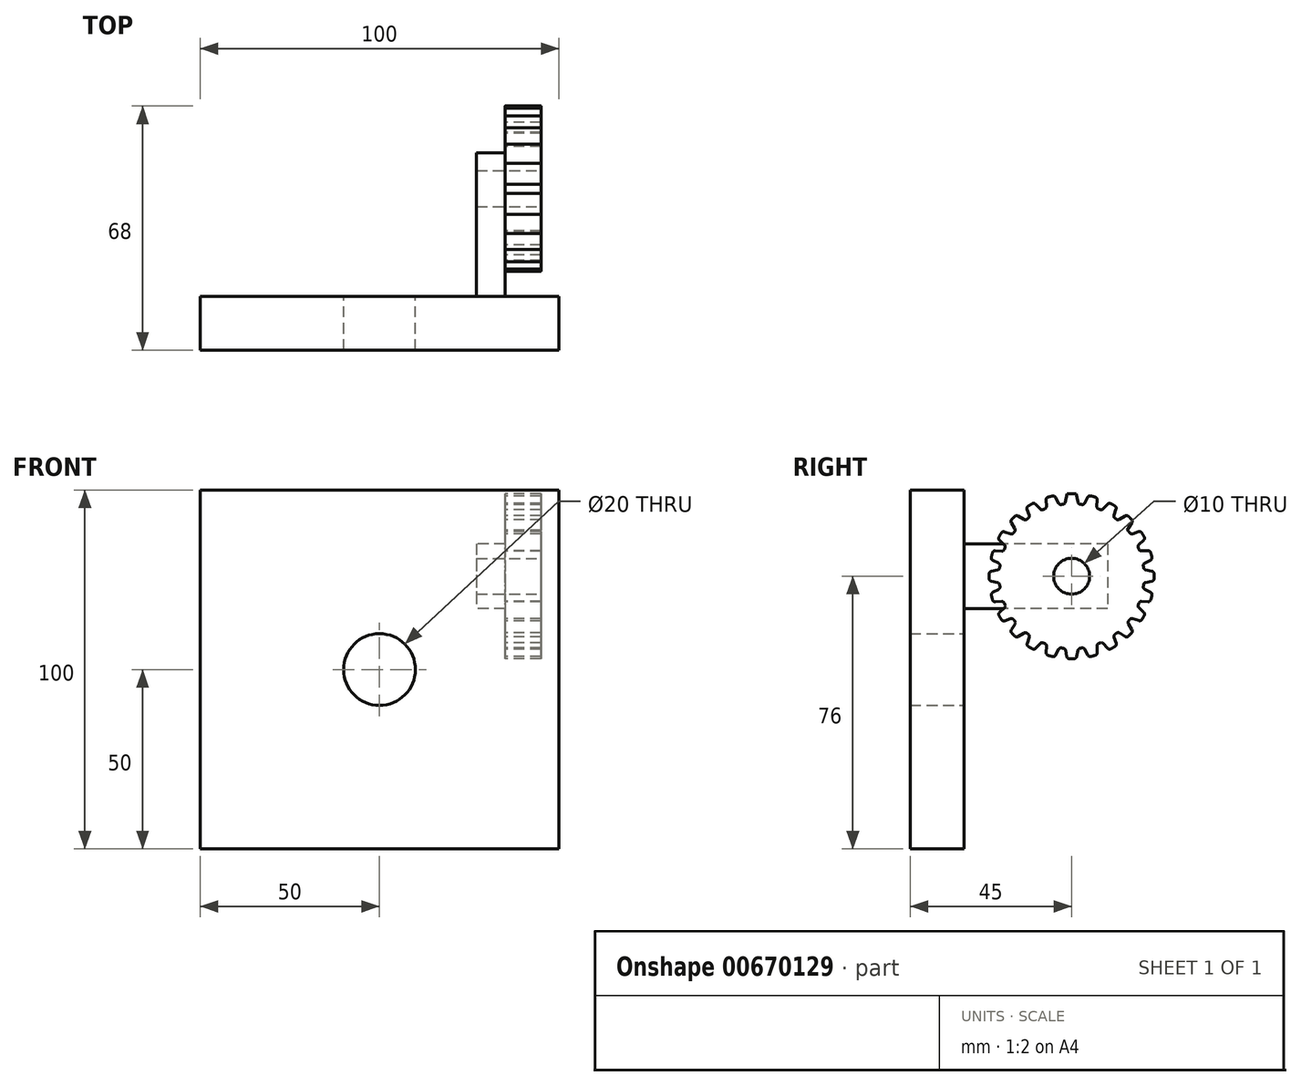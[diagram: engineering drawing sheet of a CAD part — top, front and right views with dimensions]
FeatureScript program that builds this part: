
annotation { "Feature Type Name" : "Feature", "Feature Type Description" : "" }
export const myFeature = defineFeature(function(context is Context, id is Id, definition is map)
    precondition{}
    {
        {
            var Q0;
            Q0=qCreatedBy(makeId("Front.planeOp"),FACE);
            var sketch = newSketch(context, id + "F0", { "sketchPlane" : qUnion([Q0])});
            skLineSegment(sketch, "E0", {"start": v(0, 0) * mm, "end": v(0, 100) * mm});
            skLineSegment(sketch, "E1", {"start": v(0, 100) * mm, "end": v(100, 100) * mm});
            skLineSegment(sketch, "E2", {"start": v(100, 100) * mm, "end": v(100, 0) * mm});
            skLineSegment(sketch, "E3", {"start": v(100, 0) * mm, "end": v(0, 0) * mm});
            skLineSegment(sketch, "E4", {"start": v(0, 0) * mm, "end": v(100, 0) * mm});
            skCircle(sketch, "E5", {"center": v(50, 50) * mm, "radius": 10 * mm});
            skPoint(sketch, "E6.end.orphan", {"position": v(50, 0) * mm});
            skPoint(sketch, "E6.start.orphan", {"position": v(0, 50) * mm});
            skSolve(sketch);
        }
        {
            var Q0;
            Q0 = qSketchRegion(id + "F0", true);
            extrude(context, id + "F1", {"entities" : qUnion([Q0]), "depth" : 15 * mm, "offsetDistance" : 25 * mm});
        }
        {
            var Q0;
            Q0=makeQuery(id+"F1.opExtrude","CAP_FACE",FACE,{"disambiguationData":[OSD([sQuery(id+"F0.wireOp",EDGE,"E0"),sQuery(id+"F0.wireOp",EDGE,"E1"),sQuery(id+"F0.wireOp",EDGE,"E2"),sQuery(id+"F0.wireOp",EDGE,"E4"),sQuery(id+"F0.wireOp",EDGE,"E5")])],"isStart":true});
            var sketch = newSketch(context, id + "F2", { "sketchPlane" : qUnion([Q0])});
            skLineSegment(sketch, "E7.bottom", {"start": v(-100, 100) * mm, "end": v(-85, 100) * mm});
            skLineSegment(sketch, "E7.top", {"start": v(-100, 85) * mm, "end": v(-85, 85) * mm});
            skLineSegment(sketch, "E7.left", {"start": v(-100, 100) * mm, "end": v(-100, 85) * mm});
            skLineSegment(sketch, "E7.right", {"start": v(-85, 100) * mm, "end": v(-85, 85) * mm});
            skLineSegment(sketch, "E8.bottom", {"start": v(-85, 85) * mm, "end": v(-77, 85) * mm});
            skLineSegment(sketch, "E8.top", {"start": v(-85, 67) * mm, "end": v(-77, 67) * mm});
            skLineSegment(sketch, "E8.left", {"start": v(-85, 85) * mm, "end": v(-85, 67) * mm});
            skLineSegment(sketch, "E8.right", {"start": v(-77, 85) * mm, "end": v(-77, 67) * mm});
            skSolve(sketch);
        }
        {
            var Q0;
            Q0=makeQuery(id+"F2.imprint","IMPRINT",FACE,{"disambiguationData":[TD([[makeQuery(id+"F2.imprint","IMPRINT",EDGE,{"derivedFrom":sQuery(id+"F2.wireOp",EDGE,"E8.bottom")}),-1.0]])]});
            extrude(context, id + "F3", {"entities" : qUnion([Q0]), "operationType" : NewBodyOperationType.ADD, "depth" : 40 * mm, "offsetDistance" : 25 * mm});
        }
        {
            var Q0;
            Q0=makeQuery(id+"F3.opExtrude","SWEPT_FACE",FACE,{"disambiguationData":[OSD([sQuery(id+"F2.wireOp",EDGE,"E8.left")])]});
            var sketch = newSketch(context, id + "F4", { "sketchPlane" : qUnion([Q0])});
            skLineSegment(sketch, "E9", {"start": v(40, 76) * mm, "end": v(30, 76) * mm});
            skCircle(sketch, "E10", {"center": v(30, 76) * mm, "radius": 5 * mm});
            skSolve(sketch);
        }
        {
            var Q0;
            Q0 = qSketchRegion(id + "F4", true);
            extrude(context, id + "F5", {"entities" : qUnion([Q0]), "operationType" : NewBodyOperationType.REMOVE, "oppositeDirection" : true, "depth" : 25 * mm, "offsetDistance" : 25 * mm});
        }
        {
            var Q0;
            Q0=makeQuery(id+"F3.opExtrude","SWEPT_FACE",FACE,{"disambiguationData":[OSD([sQuery(id+"F2.wireOp",EDGE,"E8.left")])]});
            var sketch = newSketch(context, id + "F6", { "sketchPlane" : qUnion([Q0])});
            skCircle(sketch, "E11.0", {"center": v(30, 76) * mm, "radius": 5 * mm});
            skCircle(sketch, "E12.0", {"center": v(30, 76) * mm, "radius": 23 * mm});
            skSolve(sketch);
        }
        {
            var Q0;
            Q0 = qSketchRegion(id + "F6", true);
            extrude(context, id + "F7", {"entities" : qUnion([Q0]), "operationType" : NewBodyOperationType.ADD, "depth" : 10 * mm, "offsetDistance" : 25 * mm});
        }
        {
            var Q0;
            Q0=makeQuery(id+"F7.opExtrude","CAP_FACE",FACE,{"disambiguationData":[OSD([sQuery(id+"F6.wireOp",EDGE,"E11.0"),sQuery(id+"F6.wireOp",EDGE,"E12.0")])],"isStart":false});
            var sketch = newSketch(context, id + "F8", { "sketchPlane" : qUnion([Q0])});
            skCircle(sketch, "E13.0.0", {"center": v(30, 76) * mm, "radius": 23 * mm});
            skLineSegment(sketch, "E14", {"start": v(30, 76) * mm, "end": v(10.07, 87.48) * mm, "construction": true});
            skLineSegment(sketch, "E15", {"start": v(10.07, 87.48) * mm, "end": v(10.72, 88.55) * mm});
            skLineSegment(sketch, "E16", {"start": v(10.72, 88.55) * mm, "end": v(13.56, 87.63) * mm});
            skLineSegment(sketch, "E17.MirrorCS", {"start": v(9.48, 86.38) * mm, "end": v(11.7, 84.39) * mm});
            skLineSegment(sketch, "E18.MirrorCS", {"start": v(10.07, 87.48) * mm, "end": v(9.48, 86.38) * mm});
            skLineSegment(sketch, "E19.1.0", {"start": v(14.63, 93.1) * mm, "end": v(17.13, 91.49) * mm});
            skLineSegment(sketch, "E19.1.1", {"start": v(13.72, 92.25) * mm, "end": v(14.63, 93.1) * mm});
            skLineSegment(sketch, "E19.1.2", {"start": v(13.72, 92.25) * mm, "end": v(12.86, 91.34) * mm});
            skLineSegment(sketch, "E19.1.3", {"start": v(12.86, 91.34) * mm, "end": v(14.49, 88.84) * mm});
            skLineSegment(sketch, "E19.2.0", {"start": v(19.58, 96.5) * mm, "end": v(21.58, 94.3) * mm});
            skLineSegment(sketch, "E19.2.1", {"start": v(18.48, 95.9) * mm, "end": v(19.58, 96.5) * mm});
            skLineSegment(sketch, "E19.2.2", {"start": v(18.48, 95.9) * mm, "end": v(17.42, 95.25) * mm});
            skLineSegment(sketch, "E19.2.3", {"start": v(17.42, 95.25) * mm, "end": v(18.34, 92.42) * mm});
            skLineSegment(sketch, "E19.3.0", {"start": v(25.24, 98.5) * mm, "end": v(26.6, 95.85) * mm});
            skLineSegment(sketch, "E19.3.1", {"start": v(24.02, 98.21) * mm, "end": v(25.24, 98.5) * mm});
            skLineSegment(sketch, "E19.3.2", {"start": v(24.02, 98.21) * mm, "end": v(22.83, 97.85) * mm});
            skLineSegment(sketch, "E19.3.3", {"start": v(22.83, 97.85) * mm, "end": v(22.99, 94.88) * mm});
            skLineSegment(sketch, "E19.4.0", {"start": v(31.23, 98.97) * mm, "end": v(31.85, 96.05) * mm});
            skLineSegment(sketch, "E19.4.1", {"start": v(29.98, 99) * mm, "end": v(31.23, 98.97) * mm});
            skLineSegment(sketch, "E19.4.2", {"start": v(29.98, 99) * mm, "end": v(28.73, 98.96) * mm});
            skLineSegment(sketch, "E19.4.3", {"start": v(28.73, 98.96) * mm, "end": v(28.1, 96.05) * mm});
            skLineSegment(sketch, "E19.5.0", {"start": v(37.13, 97.87) * mm, "end": v(36.98, 94.89) * mm});
            skLineSegment(sketch, "E19.5.1", {"start": v(35.93, 98.22) * mm, "end": v(37.13, 97.87) * mm});
            skLineSegment(sketch, "E19.5.2", {"start": v(35.93, 98.22) * mm, "end": v(34.71, 98.51) * mm});
            skLineSegment(sketch, "E19.5.3", {"start": v(34.71, 98.51) * mm, "end": v(33.36, 95.85) * mm});
            skLineSegment(sketch, "E19.6.0", {"start": v(42.55, 95.28) * mm, "end": v(41.63, 92.44) * mm});
            skLineSegment(sketch, "E19.6.1", {"start": v(41.48, 95.93) * mm, "end": v(42.55, 95.28) * mm});
            skLineSegment(sketch, "E19.6.2", {"start": v(41.48, 95.93) * mm, "end": v(40.38, 96.52) * mm});
            skLineSegment(sketch, "E19.6.3", {"start": v(40.38, 96.52) * mm, "end": v(38.39, 94.3) * mm});
            skLineSegment(sketch, "E19.7.0", {"start": v(47.1, 91.37) * mm, "end": v(45.49, 88.87) * mm});
            skLineSegment(sketch, "E19.7.1", {"start": v(46.25, 92.28) * mm, "end": v(47.1, 91.37) * mm});
            skLineSegment(sketch, "E19.7.2", {"start": v(46.25, 92.28) * mm, "end": v(45.34, 93.14) * mm});
            skLineSegment(sketch, "E19.7.3", {"start": v(45.34, 93.14) * mm, "end": v(42.84, 91.51) * mm});
            skLineSegment(sketch, "E19.8.0", {"start": v(50.5, 86.42) * mm, "end": v(48.3, 84.42) * mm});
            skLineSegment(sketch, "E19.8.1", {"start": v(49.9, 87.52) * mm, "end": v(50.5, 86.42) * mm});
            skLineSegment(sketch, "E19.8.2", {"start": v(49.9, 87.52) * mm, "end": v(49.25, 88.58) * mm});
            skLineSegment(sketch, "E19.8.3", {"start": v(49.25, 88.58) * mm, "end": v(46.42, 87.66) * mm});
            skLineSegment(sketch, "E19.9.0", {"start": v(52.5, 80.76) * mm, "end": v(49.85, 79.4) * mm});
            skLineSegment(sketch, "E19.9.1", {"start": v(52.21, 81.98) * mm, "end": v(52.5, 80.76) * mm});
            skLineSegment(sketch, "E19.9.2", {"start": v(52.21, 81.98) * mm, "end": v(51.85, 83.17) * mm});
            skLineSegment(sketch, "E19.9.3", {"start": v(51.85, 83.17) * mm, "end": v(48.88, 83.01) * mm});
            skLineSegment(sketch, "E19.10.0", {"start": v(52.97, 74.77) * mm, "end": v(50.05, 74.15) * mm});
            skLineSegment(sketch, "E19.10.1", {"start": v(53, 76.02) * mm, "end": v(52.97, 74.77) * mm});
            skLineSegment(sketch, "E19.10.2", {"start": v(53, 76.02) * mm, "end": v(52.96, 77.27) * mm});
            skLineSegment(sketch, "E19.10.3", {"start": v(52.96, 77.27) * mm, "end": v(50.05, 77.9) * mm});
            skLineSegment(sketch, "E19.11.0", {"start": v(51.87, 68.87) * mm, "end": v(48.89, 69.02) * mm});
            skLineSegment(sketch, "E19.11.1", {"start": v(52.22, 70.07) * mm, "end": v(51.87, 68.87) * mm});
            skLineSegment(sketch, "E19.11.2", {"start": v(52.22, 70.07) * mm, "end": v(52.51, 71.29) * mm});
            skLineSegment(sketch, "E19.11.3", {"start": v(52.51, 71.29) * mm, "end": v(49.85, 72.64) * mm});
            skLineSegment(sketch, "E19.12.0", {"start": v(49.28, 63.45) * mm, "end": v(46.44, 64.37) * mm});
            skLineSegment(sketch, "E19.12.1", {"start": v(49.93, 64.52) * mm, "end": v(49.28, 63.45) * mm});
            skLineSegment(sketch, "E19.12.2", {"start": v(49.93, 64.52) * mm, "end": v(50.52, 65.62) * mm});
            skLineSegment(sketch, "E19.12.3", {"start": v(50.52, 65.62) * mm, "end": v(48.3, 67.61) * mm});
            skLineSegment(sketch, "E19.13.0", {"start": v(45.37, 58.9) * mm, "end": v(42.87, 60.51) * mm});
            skLineSegment(sketch, "E19.13.1", {"start": v(46.28, 59.75) * mm, "end": v(45.37, 58.9) * mm});
            skLineSegment(sketch, "E19.13.2", {"start": v(46.28, 59.75) * mm, "end": v(47.14, 60.66) * mm});
            skLineSegment(sketch, "E19.13.3", {"start": v(47.14, 60.66) * mm, "end": v(45.51, 63.16) * mm});
            skLineSegment(sketch, "E19.14.0", {"start": v(40.42, 55.5) * mm, "end": v(38.42, 57.7) * mm});
            skLineSegment(sketch, "E19.14.1", {"start": v(41.52, 56.1) * mm, "end": v(40.42, 55.5) * mm});
            skLineSegment(sketch, "E19.14.2", {"start": v(41.52, 56.1) * mm, "end": v(42.58, 56.75) * mm});
            skLineSegment(sketch, "E19.14.3", {"start": v(42.58, 56.75) * mm, "end": v(41.66, 59.58) * mm});
            skLineSegment(sketch, "E19.15.0", {"start": v(34.76, 53.5) * mm, "end": v(33.4, 56.15) * mm});
            skLineSegment(sketch, "E19.15.1", {"start": v(35.98, 53.79) * mm, "end": v(34.76, 53.5) * mm});
            skLineSegment(sketch, "E19.15.2", {"start": v(35.98, 53.79) * mm, "end": v(37.17, 54.15) * mm});
            skLineSegment(sketch, "E19.15.3", {"start": v(37.17, 54.15) * mm, "end": v(37.01, 57.12) * mm});
            skLineSegment(sketch, "E19.16.0", {"start": v(28.77, 53.03) * mm, "end": v(28.15, 55.95) * mm});
            skLineSegment(sketch, "E19.16.1", {"start": v(30.02, 53) * mm, "end": v(28.77, 53.03) * mm});
            skLineSegment(sketch, "E19.16.2", {"start": v(30.02, 53) * mm, "end": v(31.27, 53.04) * mm});
            skLineSegment(sketch, "E19.16.3", {"start": v(31.27, 53.04) * mm, "end": v(31.9, 55.95) * mm});
            skLineSegment(sketch, "E19.17.0", {"start": v(22.87, 54.13) * mm, "end": v(23.02, 57.11) * mm});
            skLineSegment(sketch, "E19.17.1", {"start": v(24.07, 53.78) * mm, "end": v(22.87, 54.13) * mm});
            skLineSegment(sketch, "E19.17.2", {"start": v(24.07, 53.78) * mm, "end": v(25.29, 53.49) * mm});
            skLineSegment(sketch, "E19.17.3", {"start": v(25.29, 53.49) * mm, "end": v(26.64, 56.15) * mm});
            skLineSegment(sketch, "E19.18.0", {"start": v(17.45, 56.72) * mm, "end": v(18.37, 59.56) * mm});
            skLineSegment(sketch, "E19.18.1", {"start": v(18.52, 56.07) * mm, "end": v(17.45, 56.72) * mm});
            skLineSegment(sketch, "E19.18.2", {"start": v(18.52, 56.07) * mm, "end": v(19.62, 55.48) * mm});
            skLineSegment(sketch, "E19.18.3", {"start": v(19.62, 55.48) * mm, "end": v(21.61, 57.7) * mm});
            skLineSegment(sketch, "E19.19.0", {"start": v(12.9, 60.63) * mm, "end": v(14.51, 63.13) * mm});
            skLineSegment(sketch, "E19.19.1", {"start": v(13.75, 59.72) * mm, "end": v(12.9, 60.63) * mm});
            skLineSegment(sketch, "E19.19.2", {"start": v(13.75, 59.72) * mm, "end": v(14.66, 58.86) * mm});
            skLineSegment(sketch, "E19.19.3", {"start": v(14.66, 58.86) * mm, "end": v(17.16, 60.49) * mm});
            skLineSegment(sketch, "E19.20.0", {"start": v(9.5, 65.58) * mm, "end": v(11.7, 67.58) * mm});
            skLineSegment(sketch, "E19.20.1", {"start": v(10.1, 64.48) * mm, "end": v(9.5, 65.58) * mm});
            skLineSegment(sketch, "E19.20.2", {"start": v(10.1, 64.48) * mm, "end": v(10.75, 63.42) * mm});
            skLineSegment(sketch, "E19.20.3", {"start": v(10.75, 63.42) * mm, "end": v(13.58, 64.34) * mm});
            skLineSegment(sketch, "E19.21.0", {"start": v(7.5, 71.24) * mm, "end": v(10.15, 72.6) * mm});
            skLineSegment(sketch, "E19.21.1", {"start": v(7.79, 70.02) * mm, "end": v(7.5, 71.24) * mm});
            skLineSegment(sketch, "E19.21.2", {"start": v(7.79, 70.02) * mm, "end": v(8.15, 68.83) * mm});
            skLineSegment(sketch, "E19.21.3", {"start": v(8.15, 68.83) * mm, "end": v(11.12, 68.99) * mm});
            skLineSegment(sketch, "E19.22.0", {"start": v(7.03, 77.23) * mm, "end": v(9.95, 77.85) * mm});
            skLineSegment(sketch, "E19.22.1", {"start": v(7, 75.98) * mm, "end": v(7.03, 77.23) * mm});
            skLineSegment(sketch, "E19.22.2", {"start": v(7, 75.98) * mm, "end": v(7.04, 74.73) * mm});
            skLineSegment(sketch, "E19.22.3", {"start": v(7.04, 74.73) * mm, "end": v(9.95, 74.1) * mm});
            skLineSegment(sketch, "E19.23.0", {"start": v(8.13, 83.13) * mm, "end": v(11.11, 82.98) * mm});
            skLineSegment(sketch, "E19.23.1", {"start": v(7.78, 81.93) * mm, "end": v(8.13, 83.13) * mm});
            skLineSegment(sketch, "E19.23.2", {"start": v(7.78, 81.93) * mm, "end": v(7.49, 80.71) * mm});
            skLineSegment(sketch, "E19.23.3", {"start": v(7.49, 80.71) * mm, "end": v(10.15, 79.36) * mm});
            skLineSegment(sketch, "E19.anchor1", {"start": v(30, 76) * mm, "end": v(13.56, 87.63) * mm, "construction": true});
            skLineSegment(sketch, "E19.anchor2", {"start": v(30, 76) * mm, "end": v(13.56, 87.63) * mm, "construction": true});
            skArc(sketch, "E20", {"start": v(14.49, 88.84) * mm, "mid": v(13.97, 88.27) * mm, "end": v(13.56, 87.63) * mm});
            skArc(sketch, "E21.1.0", {"start": v(11.7, 84.39) * mm, "mid": v(11.34, 83.7) * mm, "end": v(11.11, 82.98) * mm});
            skArc(sketch, "E21.2.0", {"start": v(10.15, 79.36) * mm, "mid": v(9.98, 78.62) * mm, "end": v(9.95, 77.85) * mm});
            skArc(sketch, "E21.3.0", {"start": v(9.95, 74.1) * mm, "mid": v(9.99, 73.34) * mm, "end": v(10.15, 72.6) * mm});
            skArc(sketch, "E21.4.0", {"start": v(11.12, 68.99) * mm, "mid": v(11.35, 68.25) * mm, "end": v(11.7, 67.58) * mm});
            skArc(sketch, "E21.5.0", {"start": v(13.58, 64.34) * mm, "mid": v(14, 63.7) * mm, "end": v(14.51, 63.13) * mm});
            skArc(sketch, "E21.6.0", {"start": v(17.16, 60.49) * mm, "mid": v(17.73, 59.97) * mm, "end": v(18.37, 59.56) * mm});
            skArc(sketch, "E21.7.0", {"start": v(21.61, 57.7) * mm, "mid": v(22.3, 57.34) * mm, "end": v(23.02, 57.11) * mm});
            skArc(sketch, "E21.8.0", {"start": v(26.64, 56.15) * mm, "mid": v(27.38, 55.98) * mm, "end": v(28.15, 55.95) * mm});
            skArc(sketch, "E21.9.0", {"start": v(31.9, 55.95) * mm, "mid": v(32.66, 55.99) * mm, "end": v(33.4, 56.15) * mm});
            skArc(sketch, "E21.10.0", {"start": v(37.01, 57.12) * mm, "mid": v(37.75, 57.35) * mm, "end": v(38.42, 57.7) * mm});
            skArc(sketch, "E21.11.0", {"start": v(41.66, 59.58) * mm, "mid": v(42.3, 60) * mm, "end": v(42.87, 60.51) * mm});
            skArc(sketch, "E21.12.0", {"start": v(45.51, 63.16) * mm, "mid": v(46.03, 63.73) * mm, "end": v(46.44, 64.37) * mm});
            skArc(sketch, "E21.13.0", {"start": v(48.3, 67.61) * mm, "mid": v(48.66, 68.3) * mm, "end": v(48.89, 69.02) * mm});
            skArc(sketch, "E21.14.0", {"start": v(49.85, 72.64) * mm, "mid": v(50.02, 73.38) * mm, "end": v(50.05, 74.15) * mm});
            skArc(sketch, "E21.15.0", {"start": v(50.05, 77.9) * mm, "mid": v(50.01, 78.66) * mm, "end": v(49.85, 79.4) * mm});
            skArc(sketch, "E21.16.0", {"start": v(48.88, 83.01) * mm, "mid": v(48.65, 83.75) * mm, "end": v(48.3, 84.42) * mm});
            skArc(sketch, "E21.17.0", {"start": v(46.42, 87.66) * mm, "mid": v(46, 88.3) * mm, "end": v(45.49, 88.87) * mm});
            skArc(sketch, "E21.18.0", {"start": v(42.84, 91.51) * mm, "mid": v(42.27, 92.03) * mm, "end": v(41.63, 92.44) * mm});
            skArc(sketch, "E21.19.0", {"start": v(38.39, 94.3) * mm, "mid": v(37.7, 94.66) * mm, "end": v(36.98, 94.89) * mm});
            skArc(sketch, "E21.20.0", {"start": v(33.36, 95.85) * mm, "mid": v(32.62, 96.02) * mm, "end": v(31.85, 96.05) * mm});
            skArc(sketch, "E21.21.0", {"start": v(28.1, 96.05) * mm, "mid": v(27.34, 96.01) * mm, "end": v(26.6, 95.85) * mm});
            skArc(sketch, "E21.22.0", {"start": v(22.99, 94.88) * mm, "mid": v(22.25, 94.65) * mm, "end": v(21.58, 94.3) * mm});
            skArc(sketch, "E21.23.0", {"start": v(18.34, 92.42) * mm, "mid": v(17.7, 92) * mm, "end": v(17.13, 91.49) * mm});
            skLineSegment(sketch, "E22", {"start": v(11.7, 84.39) * mm, "end": v(13.56, 87.63) * mm, "construction": true});
            skLineSegment(sketch, "E23", {"start": v(12.63, 86) * mm, "end": v(10.07, 87.48) * mm});
            skSolve(sketch);
        }
        {
            var Q0;
            {var subQ0=sQuery(id+"F8.wireOp",EDGE,"E19.4.0");Q0=makeQuery(id+"F8.imprint","IMPRINT",FACE,{"disambiguationData":[TD([[makeQuery(id+"F8.imprint","IMPRINT",EDGE,{"derivedFrom":subQ0}),1.0]])]});}
            var Q1;
            {var subQ0=sQuery(id+"F8.wireOp",EDGE,"E19.5.0");Q1=makeQuery(id+"F8.imprint","IMPRINT",FACE,{"disambiguationData":[TD([[makeQuery(id+"F8.imprint","IMPRINT",EDGE,{"derivedFrom":subQ0}),1.0]])]});}
            var Q2;
            {var subQ0=sQuery(id+"F8.wireOp",EDGE,"E19.6.0");Q2=makeQuery(id+"F8.imprint","IMPRINT",FACE,{"disambiguationData":[TD([[makeQuery(id+"F8.imprint","IMPRINT",EDGE,{"derivedFrom":subQ0}),1.0]])]});}
            var Q3;
            {var subQ0=sQuery(id+"F8.wireOp",EDGE,"E19.7.0");Q3=makeQuery(id+"F8.imprint","IMPRINT",FACE,{"disambiguationData":[TD([[makeQuery(id+"F8.imprint","IMPRINT",EDGE,{"derivedFrom":subQ0}),1.0]])]});}
            var Q4;
            {var subQ0=sQuery(id+"F8.wireOp",EDGE,"E19.8.0");Q4=makeQuery(id+"F8.imprint","IMPRINT",FACE,{"disambiguationData":[TD([[makeQuery(id+"F8.imprint","IMPRINT",EDGE,{"derivedFrom":subQ0}),1.0]])]});}
            var Q5;
            {var subQ0=sQuery(id+"F8.wireOp",EDGE,"E19.9.0");Q5=makeQuery(id+"F8.imprint","IMPRINT",FACE,{"disambiguationData":[TD([[makeQuery(id+"F8.imprint","IMPRINT",EDGE,{"derivedFrom":subQ0}),1.0]])]});}
            var Q6;
            {var subQ0=sQuery(id+"F8.wireOp",EDGE,"E19.10.0");Q6=makeQuery(id+"F8.imprint","IMPRINT",FACE,{"disambiguationData":[TD([[makeQuery(id+"F8.imprint","IMPRINT",EDGE,{"derivedFrom":subQ0}),1.0]])]});}
            var Q7;
            {var subQ0=sQuery(id+"F8.wireOp",EDGE,"E19.11.0");Q7=makeQuery(id+"F8.imprint","IMPRINT",FACE,{"disambiguationData":[TD([[makeQuery(id+"F8.imprint","IMPRINT",EDGE,{"derivedFrom":subQ0}),1.0]])]});}
            var Q8;
            {var subQ0=sQuery(id+"F8.wireOp",EDGE,"E19.12.0");Q8=makeQuery(id+"F8.imprint","IMPRINT",FACE,{"disambiguationData":[TD([[makeQuery(id+"F8.imprint","IMPRINT",EDGE,{"derivedFrom":subQ0}),1.0]])]});}
            var Q9;
            {var subQ0=sQuery(id+"F8.wireOp",EDGE,"E19.13.0");Q9=makeQuery(id+"F8.imprint","IMPRINT",FACE,{"disambiguationData":[TD([[makeQuery(id+"F8.imprint","IMPRINT",EDGE,{"derivedFrom":subQ0}),1.0]])]});}
            var Q10;
            {var subQ0=sQuery(id+"F8.wireOp",EDGE,"E19.14.0");Q10=makeQuery(id+"F8.imprint","IMPRINT",FACE,{"disambiguationData":[TD([[makeQuery(id+"F8.imprint","IMPRINT",EDGE,{"derivedFrom":subQ0}),1.0]])]});}
            var Q11;
            {var subQ0=sQuery(id+"F8.wireOp",EDGE,"E19.15.0");Q11=makeQuery(id+"F8.imprint","IMPRINT",FACE,{"disambiguationData":[TD([[makeQuery(id+"F8.imprint","IMPRINT",EDGE,{"derivedFrom":subQ0}),1.0]])]});}
            var Q12;
            {var subQ0=sQuery(id+"F8.wireOp",EDGE,"E19.16.0");Q12=makeQuery(id+"F8.imprint","IMPRINT",FACE,{"disambiguationData":[TD([[makeQuery(id+"F8.imprint","IMPRINT",EDGE,{"derivedFrom":subQ0}),1.0]])]});}
            var Q13;
            {var subQ0=sQuery(id+"F8.wireOp",EDGE,"E19.18.0");Q13=makeQuery(id+"F8.imprint","IMPRINT",FACE,{"disambiguationData":[TD([[makeQuery(id+"F8.imprint","IMPRINT",EDGE,{"derivedFrom":subQ0}),1.0]])]});}
            var Q14;
            {var subQ0=sQuery(id+"F8.wireOp",EDGE,"E19.19.0");Q14=makeQuery(id+"F8.imprint","IMPRINT",FACE,{"disambiguationData":[TD([[makeQuery(id+"F8.imprint","IMPRINT",EDGE,{"derivedFrom":subQ0}),1.0]])]});}
            var Q15;
            {var subQ0=sQuery(id+"F8.wireOp",EDGE,"E19.20.0");Q15=makeQuery(id+"F8.imprint","IMPRINT",FACE,{"disambiguationData":[TD([[makeQuery(id+"F8.imprint","IMPRINT",EDGE,{"derivedFrom":subQ0}),1.0]])]});}
            var Q16;
            {var subQ0=sQuery(id+"F8.wireOp",EDGE,"E19.21.0");Q16=makeQuery(id+"F8.imprint","IMPRINT",FACE,{"disambiguationData":[TD([[makeQuery(id+"F8.imprint","IMPRINT",EDGE,{"derivedFrom":subQ0}),1.0]])]});}
            var Q17;
            {var subQ0=sQuery(id+"F8.wireOp",EDGE,"E19.22.0");Q17=makeQuery(id+"F8.imprint","IMPRINT",FACE,{"disambiguationData":[TD([[makeQuery(id+"F8.imprint","IMPRINT",EDGE,{"derivedFrom":subQ0}),1.0]])]});}
            var Q18;
            {var subQ0=sQuery(id+"F8.wireOp",EDGE,"E19.23.0");Q18=makeQuery(id+"F8.imprint","IMPRINT",FACE,{"disambiguationData":[TD([[makeQuery(id+"F8.imprint","IMPRINT",EDGE,{"derivedFrom":subQ0}),1.0]])]});}
            var Q19;
            {var subQ0=sQuery(id+"F8.wireOp",EDGE,"E19.1.3");Q19=makeQuery(id+"F8.imprint","IMPRINT",FACE,{"disambiguationData":[TD([[makeQuery(id+"F8.imprint","IMPRINT",EDGE,{"derivedFrom":subQ0}),-1.0]])]});}
            var Q20;
            {var subQ0=sQuery(id+"F8.wireOp",EDGE,"E19.1.0");Q20=makeQuery(id+"F8.imprint","IMPRINT",FACE,{"disambiguationData":[TD([[makeQuery(id+"F8.imprint","IMPRINT",EDGE,{"derivedFrom":subQ0}),1.0]])]});}
            var Q21;
            {var subQ0=sQuery(id+"F8.wireOp",EDGE,"E19.2.0");Q21=makeQuery(id+"F8.imprint","IMPRINT",FACE,{"disambiguationData":[TD([[makeQuery(id+"F8.imprint","IMPRINT",EDGE,{"derivedFrom":subQ0}),1.0]])]});}
            var Q22;
            {var subQ0=sQuery(id+"F8.wireOp",EDGE,"E19.3.0");Q22=makeQuery(id+"F8.imprint","IMPRINT",FACE,{"disambiguationData":[TD([[makeQuery(id+"F8.imprint","IMPRINT",EDGE,{"derivedFrom":subQ0}),1.0]])]});}
            var Q23;
            {var subQ0=sQuery(id+"F8.wireOp",EDGE,"E19.17.0");Q23=makeQuery(id+"F8.imprint","IMPRINT",FACE,{"disambiguationData":[TD([[makeQuery(id+"F8.imprint","IMPRINT",EDGE,{"derivedFrom":subQ0}),1.0]])]});}
            extrude(context, id + "F9", {"entities" : qUnion([Q0, Q1, Q2, Q3, Q4, Q5, Q6, Q7, Q8, Q9, Q10, Q11, Q12, Q13, Q14, Q15, Q16, Q17, Q18, Q19, Q20, Q21, Q22, Q23]), "operationType" : NewBodyOperationType.REMOVE, "oppositeDirection" : true, "depth" : 10 * mm, "hasOffset" : true, "offsetDistance" : 25 * mm, "hasDraft" : true, "draftAngle" : 0 * degree});
        }
        {
            var Q0;
            Q0=makeQuery(id+"F9.boolean.opBoolean","COPY",EDGE,{"derivedFrom":makeQuery(id+"F9.opExtrude","SWEPT_EDGE",EDGE,{"disambiguationData":[OSD([sQuery(id+"F8.wireOp",EDGE,"E13.0.0"),sQuery(id+"F8.wireOp",EDGE,"E16"),sQuery(id+"F8.wireOp",EDGE,"E15")])]})});
            var Q1;
            Q1=makeQuery(id+"F9.boolean.opBoolean","COPY",EDGE,{"derivedFrom":makeQuery(id+"F9.opExtrude","SWEPT_EDGE",EDGE,{"disambiguationData":[OSD([sQuery(id+"F8.wireOp",EDGE,"E13.0.0"),sQuery(id+"F8.wireOp",EDGE,"E19.1.0"),sQuery(id+"F8.wireOp",EDGE,"E19.1.1")])]})});
            var Q2;
            Q2=makeQuery(id+"F9.boolean.opBoolean","COPY",EDGE,{"derivedFrom":makeQuery(id+"F9.opExtrude","SWEPT_EDGE",EDGE,{"disambiguationData":[OSD([sQuery(id+"F8.wireOp",EDGE,"E13.0.0"),sQuery(id+"F8.wireOp",EDGE,"E19.1.2"),sQuery(id+"F8.wireOp",EDGE,"E19.1.3")])]})});
            var Q3;
            Q3=makeQuery(id+"F9.boolean.opBoolean","COPY",EDGE,{"derivedFrom":makeQuery(id+"F9.opExtrude","SWEPT_EDGE",EDGE,{"disambiguationData":[OSD([sQuery(id+"F8.wireOp",EDGE,"E13.0.0"),sQuery(id+"F8.wireOp",EDGE,"E19.2.2"),sQuery(id+"F8.wireOp",EDGE,"E19.2.3")])]})});
            var Q4;
            Q4=makeQuery(id+"F9.boolean.opBoolean","COPY",EDGE,{"derivedFrom":makeQuery(id+"F9.opExtrude","SWEPT_EDGE",EDGE,{"disambiguationData":[OSD([sQuery(id+"F8.wireOp",EDGE,"E13.0.0"),sQuery(id+"F8.wireOp",EDGE,"E19.2.0"),sQuery(id+"F8.wireOp",EDGE,"E19.2.1")])]})});
            var Q5;
            Q5=makeQuery(id+"F9.boolean.opBoolean","COPY",EDGE,{"derivedFrom":makeQuery(id+"F9.opExtrude","SWEPT_EDGE",EDGE,{"disambiguationData":[OSD([sQuery(id+"F8.wireOp",EDGE,"E19.2.0"),sQuery(id+"F8.wireOp",EDGE,"E21.22.0")])]})});
            var Q6;
            Q6=makeQuery(id+"F9.boolean.opBoolean","COPY",EDGE,{"derivedFrom":makeQuery(id+"F9.opExtrude","SWEPT_EDGE",EDGE,{"disambiguationData":[OSD([sQuery(id+"F8.wireOp",EDGE,"E19.3.3"),sQuery(id+"F8.wireOp",EDGE,"E21.22.0")])]})});
            var Q7;
            Q7=makeQuery(id+"F9.boolean.opBoolean","COPY",EDGE,{"derivedFrom":makeQuery(id+"F9.opExtrude","SWEPT_EDGE",EDGE,{"disambiguationData":[OSD([sQuery(id+"F8.wireOp",EDGE,"E19.2.3"),sQuery(id+"F8.wireOp",EDGE,"E21.23.0")])]})});
            var Q8;
            Q8=makeQuery(id+"F9.boolean.opBoolean","COPY",EDGE,{"derivedFrom":makeQuery(id+"F9.opExtrude","SWEPT_EDGE",EDGE,{"disambiguationData":[OSD([sQuery(id+"F8.wireOp",EDGE,"E19.1.0"),sQuery(id+"F8.wireOp",EDGE,"E21.23.0")])]})});
            var Q9;
            Q9=makeQuery(id+"F9.boolean.opBoolean","COPY",EDGE,{"derivedFrom":makeQuery(id+"F9.opExtrude","SWEPT_EDGE",EDGE,{"disambiguationData":[OSD([sQuery(id+"F8.wireOp",EDGE,"E13.0.0"),sQuery(id+"F8.wireOp",EDGE,"E19.3.0"),sQuery(id+"F8.wireOp",EDGE,"E19.3.1")])]})});
            var Q10;
            Q10=makeQuery(id+"F9.boolean.opBoolean","COPY",EDGE,{"derivedFrom":makeQuery(id+"F9.opExtrude","SWEPT_EDGE",EDGE,{"disambiguationData":[OSD([sQuery(id+"F8.wireOp",EDGE,"E19.3.0"),sQuery(id+"F8.wireOp",EDGE,"E21.21.0")])]})});
            var Q11;
            Q11=makeQuery(id+"F9.boolean.opBoolean","COPY",EDGE,{"derivedFrom":makeQuery(id+"F9.opExtrude","SWEPT_EDGE",EDGE,{"disambiguationData":[OSD([sQuery(id+"F8.wireOp",EDGE,"E19.4.3"),sQuery(id+"F8.wireOp",EDGE,"E21.21.0")])]})});
            var Q12;
            Q12=makeQuery(id+"F9.boolean.opBoolean","COPY",EDGE,{"derivedFrom":makeQuery(id+"F9.opExtrude","SWEPT_EDGE",EDGE,{"disambiguationData":[OSD([sQuery(id+"F8.wireOp",EDGE,"E13.0.0"),sQuery(id+"F8.wireOp",EDGE,"E19.4.2"),sQuery(id+"F8.wireOp",EDGE,"E19.4.3")])]})});
            var Q13;
            Q13=makeQuery(id+"F9.boolean.opBoolean","COPY",EDGE,{"derivedFrom":makeQuery(id+"F9.opExtrude","SWEPT_EDGE",EDGE,{"disambiguationData":[OSD([sQuery(id+"F8.wireOp",EDGE,"E13.0.0"),sQuery(id+"F8.wireOp",EDGE,"E19.4.0"),sQuery(id+"F8.wireOp",EDGE,"E19.4.1")])]})});
            var Q14;
            Q14=makeQuery(id+"F9.boolean.opBoolean","COPY",EDGE,{"derivedFrom":makeQuery(id+"F9.opExtrude","SWEPT_EDGE",EDGE,{"disambiguationData":[OSD([sQuery(id+"F8.wireOp",EDGE,"E19.4.0"),sQuery(id+"F8.wireOp",EDGE,"E21.20.0")])]})});
            var Q15;
            Q15=makeQuery(id+"F9.boolean.opBoolean","COPY",EDGE,{"derivedFrom":makeQuery(id+"F9.opExtrude","SWEPT_EDGE",EDGE,{"disambiguationData":[OSD([sQuery(id+"F8.wireOp",EDGE,"E19.5.3"),sQuery(id+"F8.wireOp",EDGE,"E21.20.0")])]})});
            var Q16;
            Q16=makeQuery(id+"F9.boolean.opBoolean","COPY",EDGE,{"derivedFrom":makeQuery(id+"F9.opExtrude","SWEPT_EDGE",EDGE,{"disambiguationData":[OSD([sQuery(id+"F8.wireOp",EDGE,"E13.0.0"),sQuery(id+"F8.wireOp",EDGE,"E19.5.2"),sQuery(id+"F8.wireOp",EDGE,"E19.5.3")])]})});
            var Q17;
            Q17=makeQuery(id+"F9.boolean.opBoolean","COPY",EDGE,{"derivedFrom":makeQuery(id+"F9.opExtrude","SWEPT_EDGE",EDGE,{"disambiguationData":[OSD([sQuery(id+"F8.wireOp",EDGE,"E13.0.0"),sQuery(id+"F8.wireOp",EDGE,"E19.3.2"),sQuery(id+"F8.wireOp",EDGE,"E19.3.3")])]})});
            var Q18;
            Q18=makeQuery(id+"F9.boolean.opBoolean","COPY",EDGE,{"derivedFrom":makeQuery(id+"F9.opExtrude","SWEPT_EDGE",EDGE,{"disambiguationData":[OSD([sQuery(id+"F8.wireOp",EDGE,"E19.1.3"),sQuery(id+"F8.wireOp",EDGE,"E20")])]})});
            var Q19;
            Q19=makeQuery(id+"F9.boolean.opBoolean","COPY",EDGE,{"derivedFrom":makeQuery(id+"F9.opExtrude","SWEPT_EDGE",EDGE,{"disambiguationData":[OSD([sQuery(id+"F8.wireOp",EDGE,"E16"),sQuery(id+"F8.wireOp",EDGE,"E20")])]})});
            var Q20;
            Q20=makeQuery(id+"F9.boolean.opBoolean","COPY",EDGE,{"derivedFrom":makeQuery(id+"F9.opExtrude","SWEPT_EDGE",EDGE,{"disambiguationData":[OSD([sQuery(id+"F8.wireOp",EDGE,"E19.6.3"),sQuery(id+"F8.wireOp",EDGE,"E21.19.0")])]})});
            var Q21;
            Q21=makeQuery(id+"F9.boolean.opBoolean","COPY",EDGE,{"derivedFrom":makeQuery(id+"F9.opExtrude","SWEPT_EDGE",EDGE,{"disambiguationData":[OSD([sQuery(id+"F8.wireOp",EDGE,"E19.5.0"),sQuery(id+"F8.wireOp",EDGE,"E21.19.0")])]})});
            var Q22;
            Q22=makeQuery(id+"F9.boolean.opBoolean","COPY",EDGE,{"derivedFrom":makeQuery(id+"F9.opExtrude","SWEPT_EDGE",EDGE,{"disambiguationData":[OSD([sQuery(id+"F8.wireOp",EDGE,"E13.0.0"),sQuery(id+"F8.wireOp",EDGE,"E19.6.2"),sQuery(id+"F8.wireOp",EDGE,"E19.6.3")])]})});
            var Q23;
            Q23=makeQuery(id+"F9.boolean.opBoolean","COPY",EDGE,{"derivedFrom":makeQuery(id+"F9.opExtrude","SWEPT_EDGE",EDGE,{"disambiguationData":[OSD([sQuery(id+"F8.wireOp",EDGE,"E13.0.0"),sQuery(id+"F8.wireOp",EDGE,"E19.5.0"),sQuery(id+"F8.wireOp",EDGE,"E19.5.1")])]})});
            var Q24;
            Q24=makeQuery(id+"F9.boolean.opBoolean","COPY",EDGE,{"derivedFrom":makeQuery(id+"F9.opExtrude","SWEPT_EDGE",EDGE,{"disambiguationData":[OSD([sQuery(id+"F8.wireOp",EDGE,"E13.0.0"),sQuery(id+"F8.wireOp",EDGE,"E19.6.0"),sQuery(id+"F8.wireOp",EDGE,"E19.6.1")])]})});
            var Q25;
            Q25=makeQuery(id+"F9.boolean.opBoolean","COPY",EDGE,{"derivedFrom":makeQuery(id+"F9.opExtrude","SWEPT_EDGE",EDGE,{"disambiguationData":[OSD([sQuery(id+"F8.wireOp",EDGE,"E19.6.0"),sQuery(id+"F8.wireOp",EDGE,"E21.18.0")])]})});
            var Q26;
            Q26=makeQuery(id+"F9.boolean.opBoolean","COPY",EDGE,{"derivedFrom":makeQuery(id+"F9.opExtrude","SWEPT_EDGE",EDGE,{"disambiguationData":[OSD([sQuery(id+"F8.wireOp",EDGE,"E19.7.3"),sQuery(id+"F8.wireOp",EDGE,"E21.18.0")])]})});
            var Q27;
            Q27=makeQuery(id+"F9.boolean.opBoolean","COPY",EDGE,{"derivedFrom":makeQuery(id+"F9.opExtrude","SWEPT_EDGE",EDGE,{"disambiguationData":[OSD([sQuery(id+"F8.wireOp",EDGE,"E13.0.0"),sQuery(id+"F8.wireOp",EDGE,"E19.7.2"),sQuery(id+"F8.wireOp",EDGE,"E19.7.3")])]})});
            var Q28;
            Q28=makeQuery(id+"F9.boolean.opBoolean","COPY",EDGE,{"derivedFrom":makeQuery(id+"F9.opExtrude","SWEPT_EDGE",EDGE,{"disambiguationData":[OSD([sQuery(id+"F8.wireOp",EDGE,"E17.MirrorCS"),sQuery(id+"F8.wireOp",EDGE,"E21.1.0")])]})});
            var Q29;
            Q29=makeQuery(id+"F9.boolean.opBoolean","COPY",EDGE,{"derivedFrom":makeQuery(id+"F9.opExtrude","SWEPT_EDGE",EDGE,{"disambiguationData":[OSD([sQuery(id+"F8.wireOp",EDGE,"E13.0.0"),sQuery(id+"F8.wireOp",EDGE,"E18.MirrorCS"),sQuery(id+"F8.wireOp",EDGE,"E17.MirrorCS")])]})});
            var Q30;
            Q30=makeQuery(id+"F9.boolean.opBoolean","COPY",EDGE,{"derivedFrom":makeQuery(id+"F9.opExtrude","SWEPT_EDGE",EDGE,{"disambiguationData":[OSD([sQuery(id+"F8.wireOp",EDGE,"E19.23.0"),sQuery(id+"F8.wireOp",EDGE,"E21.1.0")])]})});
            var Q31;
            Q31=makeQuery(id+"F9.boolean.opBoolean","COPY",EDGE,{"derivedFrom":makeQuery(id+"F9.opExtrude","SWEPT_EDGE",EDGE,{"disambiguationData":[OSD([sQuery(id+"F8.wireOp",EDGE,"E13.0.0"),sQuery(id+"F8.wireOp",EDGE,"E19.23.0"),sQuery(id+"F8.wireOp",EDGE,"E19.23.1")])]})});
            var Q32;
            Q32=makeQuery(id+"F9.boolean.opBoolean","COPY",EDGE,{"derivedFrom":makeQuery(id+"F9.opExtrude","SWEPT_EDGE",EDGE,{"disambiguationData":[OSD([sQuery(id+"F8.wireOp",EDGE,"E13.0.0"),sQuery(id+"F8.wireOp",EDGE,"E19.23.2"),sQuery(id+"F8.wireOp",EDGE,"E19.23.3")])]})});
            var Q33;
            Q33=makeQuery(id+"F9.boolean.opBoolean","COPY",EDGE,{"derivedFrom":makeQuery(id+"F9.opExtrude","SWEPT_EDGE",EDGE,{"disambiguationData":[OSD([sQuery(id+"F8.wireOp",EDGE,"E19.23.3"),sQuery(id+"F8.wireOp",EDGE,"E21.2.0")])]})});
            var Q34;
            Q34=makeQuery(id+"F9.boolean.opBoolean","COPY",EDGE,{"derivedFrom":makeQuery(id+"F9.opExtrude","SWEPT_EDGE",EDGE,{"disambiguationData":[OSD([sQuery(id+"F8.wireOp",EDGE,"E19.22.0"),sQuery(id+"F8.wireOp",EDGE,"E21.2.0")])]})});
            var Q35;
            Q35=makeQuery(id+"F9.boolean.opBoolean","COPY",EDGE,{"derivedFrom":makeQuery(id+"F9.opExtrude","SWEPT_EDGE",EDGE,{"disambiguationData":[OSD([sQuery(id+"F8.wireOp",EDGE,"E13.0.0"),sQuery(id+"F8.wireOp",EDGE,"E19.22.0"),sQuery(id+"F8.wireOp",EDGE,"E19.22.1")])]})});
            var Q36;
            Q36=makeQuery(id+"F9.boolean.opBoolean","COPY",EDGE,{"derivedFrom":makeQuery(id+"F9.opExtrude","SWEPT_EDGE",EDGE,{"disambiguationData":[OSD([sQuery(id+"F8.wireOp",EDGE,"E13.0.0"),sQuery(id+"F8.wireOp",EDGE,"E19.22.2"),sQuery(id+"F8.wireOp",EDGE,"E19.22.3")])]})});
            var Q37;
            Q37=makeQuery(id+"F9.boolean.opBoolean","COPY",EDGE,{"derivedFrom":makeQuery(id+"F9.opExtrude","SWEPT_EDGE",EDGE,{"disambiguationData":[OSD([sQuery(id+"F8.wireOp",EDGE,"E19.22.3"),sQuery(id+"F8.wireOp",EDGE,"E21.3.0")])]})});
            var Q38;
            Q38=makeQuery(id+"F9.boolean.opBoolean","COPY",EDGE,{"derivedFrom":makeQuery(id+"F9.opExtrude","SWEPT_EDGE",EDGE,{"disambiguationData":[OSD([sQuery(id+"F8.wireOp",EDGE,"E19.21.0"),sQuery(id+"F8.wireOp",EDGE,"E21.3.0")])]})});
            var Q39;
            Q39=makeQuery(id+"F9.boolean.opBoolean","COPY",EDGE,{"derivedFrom":makeQuery(id+"F9.opExtrude","SWEPT_EDGE",EDGE,{"disambiguationData":[OSD([sQuery(id+"F8.wireOp",EDGE,"E13.0.0"),sQuery(id+"F8.wireOp",EDGE,"E19.21.0"),sQuery(id+"F8.wireOp",EDGE,"E19.21.1")])]})});
            var Q40;
            Q40=makeQuery(id+"F9.boolean.opBoolean","COPY",EDGE,{"derivedFrom":makeQuery(id+"F9.opExtrude","SWEPT_EDGE",EDGE,{"disambiguationData":[OSD([sQuery(id+"F8.wireOp",EDGE,"E13.0.0"),sQuery(id+"F8.wireOp",EDGE,"E19.21.2"),sQuery(id+"F8.wireOp",EDGE,"E19.21.3")])]})});
            var Q41;
            Q41=makeQuery(id+"F9.boolean.opBoolean","COPY",EDGE,{"derivedFrom":makeQuery(id+"F9.opExtrude","SWEPT_EDGE",EDGE,{"disambiguationData":[OSD([sQuery(id+"F8.wireOp",EDGE,"E19.21.3"),sQuery(id+"F8.wireOp",EDGE,"E21.4.0")])]})});
            var Q42;
            Q42=makeQuery(id+"F9.boolean.opBoolean","COPY",EDGE,{"derivedFrom":makeQuery(id+"F9.opExtrude","SWEPT_EDGE",EDGE,{"disambiguationData":[OSD([sQuery(id+"F8.wireOp",EDGE,"E19.20.0"),sQuery(id+"F8.wireOp",EDGE,"E21.4.0")])]})});
            var Q43;
            Q43=makeQuery(id+"F9.boolean.opBoolean","COPY",EDGE,{"derivedFrom":makeQuery(id+"F9.opExtrude","SWEPT_EDGE",EDGE,{"disambiguationData":[OSD([sQuery(id+"F8.wireOp",EDGE,"E13.0.0"),sQuery(id+"F8.wireOp",EDGE,"E19.20.0"),sQuery(id+"F8.wireOp",EDGE,"E19.20.1")])]})});
            var Q44;
            Q44=makeQuery(id+"F9.boolean.opBoolean","COPY",EDGE,{"derivedFrom":makeQuery(id+"F9.opExtrude","SWEPT_EDGE",EDGE,{"disambiguationData":[OSD([sQuery(id+"F8.wireOp",EDGE,"E13.0.0"),sQuery(id+"F8.wireOp",EDGE,"E19.20.2"),sQuery(id+"F8.wireOp",EDGE,"E19.20.3")])]})});
            var Q45;
            Q45=makeQuery(id+"F9.boolean.opBoolean","COPY",EDGE,{"derivedFrom":makeQuery(id+"F9.opExtrude","SWEPT_EDGE",EDGE,{"disambiguationData":[OSD([sQuery(id+"F8.wireOp",EDGE,"E19.20.3"),sQuery(id+"F8.wireOp",EDGE,"E21.5.0")])]})});
            var Q46;
            Q46=makeQuery(id+"F9.boolean.opBoolean","COPY",EDGE,{"derivedFrom":makeQuery(id+"F9.opExtrude","SWEPT_EDGE",EDGE,{"disambiguationData":[OSD([sQuery(id+"F8.wireOp",EDGE,"E19.19.0"),sQuery(id+"F8.wireOp",EDGE,"E21.5.0")])]})});
            var Q47;
            Q47=makeQuery(id+"F9.boolean.opBoolean","COPY",EDGE,{"derivedFrom":makeQuery(id+"F9.opExtrude","SWEPT_EDGE",EDGE,{"disambiguationData":[OSD([sQuery(id+"F8.wireOp",EDGE,"E13.0.0"),sQuery(id+"F8.wireOp",EDGE,"E19.19.0"),sQuery(id+"F8.wireOp",EDGE,"E19.19.1")])]})});
            var Q48;
            Q48=makeQuery(id+"F9.boolean.opBoolean","COPY",EDGE,{"derivedFrom":makeQuery(id+"F9.opExtrude","SWEPT_EDGE",EDGE,{"disambiguationData":[OSD([sQuery(id+"F8.wireOp",EDGE,"E13.0.0"),sQuery(id+"F8.wireOp",EDGE,"E19.19.2"),sQuery(id+"F8.wireOp",EDGE,"E19.19.3")])]})});
            var Q49;
            Q49=makeQuery(id+"F9.boolean.opBoolean","COPY",EDGE,{"derivedFrom":makeQuery(id+"F9.opExtrude","SWEPT_EDGE",EDGE,{"disambiguationData":[OSD([sQuery(id+"F8.wireOp",EDGE,"E19.19.3"),sQuery(id+"F8.wireOp",EDGE,"E21.6.0")])]})});
            var Q50;
            Q50=makeQuery(id+"F9.boolean.opBoolean","COPY",EDGE,{"derivedFrom":makeQuery(id+"F9.opExtrude","SWEPT_EDGE",EDGE,{"disambiguationData":[OSD([sQuery(id+"F8.wireOp",EDGE,"E19.18.0"),sQuery(id+"F8.wireOp",EDGE,"E21.6.0")])]})});
            var Q51;
            Q51=makeQuery(id+"F9.boolean.opBoolean","COPY",EDGE,{"derivedFrom":makeQuery(id+"F9.opExtrude","SWEPT_EDGE",EDGE,{"disambiguationData":[OSD([sQuery(id+"F8.wireOp",EDGE,"E13.0.0"),sQuery(id+"F8.wireOp",EDGE,"E19.18.0"),sQuery(id+"F8.wireOp",EDGE,"E19.18.1")])]})});
            var Q52;
            Q52=makeQuery(id+"F9.boolean.opBoolean","COPY",EDGE,{"derivedFrom":makeQuery(id+"F9.opExtrude","SWEPT_EDGE",EDGE,{"disambiguationData":[OSD([sQuery(id+"F8.wireOp",EDGE,"E13.0.0"),sQuery(id+"F8.wireOp",EDGE,"E19.18.2"),sQuery(id+"F8.wireOp",EDGE,"E19.18.3")])]})});
            var Q53;
            Q53=makeQuery(id+"F9.boolean.opBoolean","COPY",EDGE,{"derivedFrom":makeQuery(id+"F9.opExtrude","SWEPT_EDGE",EDGE,{"disambiguationData":[OSD([sQuery(id+"F8.wireOp",EDGE,"E19.18.3"),sQuery(id+"F8.wireOp",EDGE,"E21.7.0")])]})});
            var Q54;
            Q54=makeQuery(id+"F9.boolean.opBoolean","COPY",EDGE,{"derivedFrom":makeQuery(id+"F9.opExtrude","SWEPT_EDGE",EDGE,{"disambiguationData":[OSD([sQuery(id+"F8.wireOp",EDGE,"E19.17.0"),sQuery(id+"F8.wireOp",EDGE,"E21.7.0")])]})});
            var Q55;
            Q55=makeQuery(id+"F9.boolean.opBoolean","COPY",EDGE,{"derivedFrom":makeQuery(id+"F9.opExtrude","SWEPT_EDGE",EDGE,{"disambiguationData":[OSD([sQuery(id+"F8.wireOp",EDGE,"E13.0.0"),sQuery(id+"F8.wireOp",EDGE,"E19.17.0"),sQuery(id+"F8.wireOp",EDGE,"E19.17.1")])]})});
            var Q56;
            Q56=makeQuery(id+"F9.boolean.opBoolean","COPY",EDGE,{"derivedFrom":makeQuery(id+"F9.opExtrude","SWEPT_EDGE",EDGE,{"disambiguationData":[OSD([sQuery(id+"F8.wireOp",EDGE,"E19.17.3"),sQuery(id+"F8.wireOp",EDGE,"E21.8.0")])]})});
            var Q57;
            Q57=makeQuery(id+"F9.boolean.opBoolean","COPY",EDGE,{"derivedFrom":makeQuery(id+"F9.opExtrude","SWEPT_EDGE",EDGE,{"disambiguationData":[OSD([sQuery(id+"F8.wireOp",EDGE,"E13.0.0"),sQuery(id+"F8.wireOp",EDGE,"E19.17.2"),sQuery(id+"F8.wireOp",EDGE,"E19.17.3")])]})});
            var Q58;
            Q58=makeQuery(id+"F9.boolean.opBoolean","COPY",EDGE,{"derivedFrom":makeQuery(id+"F9.opExtrude","SWEPT_EDGE",EDGE,{"disambiguationData":[OSD([sQuery(id+"F8.wireOp",EDGE,"E19.16.0"),sQuery(id+"F8.wireOp",EDGE,"E21.8.0")])]})});
            var Q59;
            Q59=makeQuery(id+"F9.boolean.opBoolean","COPY",EDGE,{"derivedFrom":makeQuery(id+"F9.opExtrude","SWEPT_EDGE",EDGE,{"disambiguationData":[OSD([sQuery(id+"F8.wireOp",EDGE,"E13.0.0"),sQuery(id+"F8.wireOp",EDGE,"E19.16.0"),sQuery(id+"F8.wireOp",EDGE,"E19.16.1")])]})});
            var Q60;
            Q60=makeQuery(id+"F9.boolean.opBoolean","COPY",EDGE,{"derivedFrom":makeQuery(id+"F9.opExtrude","SWEPT_EDGE",EDGE,{"disambiguationData":[OSD([sQuery(id+"F8.wireOp",EDGE,"E13.0.0"),sQuery(id+"F8.wireOp",EDGE,"E19.16.2"),sQuery(id+"F8.wireOp",EDGE,"E19.16.3")])]})});
            var Q61;
            Q61=makeQuery(id+"F9.boolean.opBoolean","COPY",EDGE,{"derivedFrom":makeQuery(id+"F9.opExtrude","SWEPT_EDGE",EDGE,{"disambiguationData":[OSD([sQuery(id+"F8.wireOp",EDGE,"E19.16.3"),sQuery(id+"F8.wireOp",EDGE,"E21.9.0")])]})});
            var Q62;
            Q62=makeQuery(id+"F9.boolean.opBoolean","COPY",EDGE,{"derivedFrom":makeQuery(id+"F9.opExtrude","SWEPT_EDGE",EDGE,{"disambiguationData":[OSD([sQuery(id+"F8.wireOp",EDGE,"E19.15.0"),sQuery(id+"F8.wireOp",EDGE,"E21.9.0")])]})});
            var Q63;
            Q63=makeQuery(id+"F9.boolean.opBoolean","COPY",EDGE,{"derivedFrom":makeQuery(id+"F9.opExtrude","SWEPT_EDGE",EDGE,{"disambiguationData":[OSD([sQuery(id+"F8.wireOp",EDGE,"E13.0.0"),sQuery(id+"F8.wireOp",EDGE,"E19.15.0"),sQuery(id+"F8.wireOp",EDGE,"E19.15.1")])]})});
            var Q64;
            Q64=makeQuery(id+"F9.boolean.opBoolean","COPY",EDGE,{"derivedFrom":makeQuery(id+"F9.opExtrude","SWEPT_EDGE",EDGE,{"disambiguationData":[OSD([sQuery(id+"F8.wireOp",EDGE,"E13.0.0"),sQuery(id+"F8.wireOp",EDGE,"E19.15.2"),sQuery(id+"F8.wireOp",EDGE,"E19.15.3")])]})});
            var Q65;
            Q65=makeQuery(id+"F9.boolean.opBoolean","COPY",EDGE,{"derivedFrom":makeQuery(id+"F9.opExtrude","SWEPT_EDGE",EDGE,{"disambiguationData":[OSD([sQuery(id+"F8.wireOp",EDGE,"E19.15.3"),sQuery(id+"F8.wireOp",EDGE,"E21.10.0")])]})});
            var Q66;
            Q66=makeQuery(id+"F9.boolean.opBoolean","COPY",EDGE,{"derivedFrom":makeQuery(id+"F9.opExtrude","SWEPT_EDGE",EDGE,{"disambiguationData":[OSD([sQuery(id+"F8.wireOp",EDGE,"E19.14.0"),sQuery(id+"F8.wireOp",EDGE,"E21.10.0")])]})});
            var Q67;
            Q67=makeQuery(id+"F9.boolean.opBoolean","COPY",EDGE,{"derivedFrom":makeQuery(id+"F9.opExtrude","SWEPT_EDGE",EDGE,{"disambiguationData":[OSD([sQuery(id+"F8.wireOp",EDGE,"E13.0.0"),sQuery(id+"F8.wireOp",EDGE,"E19.14.0"),sQuery(id+"F8.wireOp",EDGE,"E19.14.1")])]})});
            var Q68;
            Q68=makeQuery(id+"F9.boolean.opBoolean","COPY",EDGE,{"derivedFrom":makeQuery(id+"F9.opExtrude","SWEPT_EDGE",EDGE,{"disambiguationData":[OSD([sQuery(id+"F8.wireOp",EDGE,"E13.0.0"),sQuery(id+"F8.wireOp",EDGE,"E19.14.2"),sQuery(id+"F8.wireOp",EDGE,"E19.14.3")])]})});
            var Q69;
            Q69=makeQuery(id+"F9.boolean.opBoolean","COPY",EDGE,{"derivedFrom":makeQuery(id+"F9.opExtrude","SWEPT_EDGE",EDGE,{"disambiguationData":[OSD([sQuery(id+"F8.wireOp",EDGE,"E19.14.3"),sQuery(id+"F8.wireOp",EDGE,"E21.11.0")])]})});
            var Q70;
            Q70=makeQuery(id+"F9.boolean.opBoolean","COPY",EDGE,{"derivedFrom":makeQuery(id+"F9.opExtrude","SWEPT_EDGE",EDGE,{"disambiguationData":[OSD([sQuery(id+"F8.wireOp",EDGE,"E19.13.0"),sQuery(id+"F8.wireOp",EDGE,"E21.11.0")])]})});
            var Q71;
            Q71=makeQuery(id+"F9.boolean.opBoolean","COPY",EDGE,{"derivedFrom":makeQuery(id+"F9.opExtrude","SWEPT_EDGE",EDGE,{"disambiguationData":[OSD([sQuery(id+"F8.wireOp",EDGE,"E13.0.0"),sQuery(id+"F8.wireOp",EDGE,"E19.13.0"),sQuery(id+"F8.wireOp",EDGE,"E19.13.1")])]})});
            var Q72;
            Q72=makeQuery(id+"F9.boolean.opBoolean","COPY",EDGE,{"derivedFrom":makeQuery(id+"F9.opExtrude","SWEPT_EDGE",EDGE,{"disambiguationData":[OSD([sQuery(id+"F8.wireOp",EDGE,"E13.0.0"),sQuery(id+"F8.wireOp",EDGE,"E19.13.2"),sQuery(id+"F8.wireOp",EDGE,"E19.13.3")])]})});
            var Q73;
            Q73=makeQuery(id+"F9.boolean.opBoolean","COPY",EDGE,{"derivedFrom":makeQuery(id+"F9.opExtrude","SWEPT_EDGE",EDGE,{"disambiguationData":[OSD([sQuery(id+"F8.wireOp",EDGE,"E19.13.3"),sQuery(id+"F8.wireOp",EDGE,"E21.12.0")])]})});
            var Q74;
            Q74=makeQuery(id+"F9.boolean.opBoolean","COPY",EDGE,{"derivedFrom":makeQuery(id+"F9.opExtrude","SWEPT_EDGE",EDGE,{"disambiguationData":[OSD([sQuery(id+"F8.wireOp",EDGE,"E19.12.0"),sQuery(id+"F8.wireOp",EDGE,"E21.12.0")])]})});
            var Q75;
            Q75=makeQuery(id+"F9.boolean.opBoolean","COPY",EDGE,{"derivedFrom":makeQuery(id+"F9.opExtrude","SWEPT_EDGE",EDGE,{"disambiguationData":[OSD([sQuery(id+"F8.wireOp",EDGE,"E13.0.0"),sQuery(id+"F8.wireOp",EDGE,"E19.12.0"),sQuery(id+"F8.wireOp",EDGE,"E19.12.1")])]})});
            var Q76;
            Q76=makeQuery(id+"F9.boolean.opBoolean","COPY",EDGE,{"derivedFrom":makeQuery(id+"F9.opExtrude","SWEPT_EDGE",EDGE,{"disambiguationData":[OSD([sQuery(id+"F8.wireOp",EDGE,"E13.0.0"),sQuery(id+"F8.wireOp",EDGE,"E19.12.2"),sQuery(id+"F8.wireOp",EDGE,"E19.12.3")])]})});
            var Q77;
            Q77=makeQuery(id+"F9.boolean.opBoolean","COPY",EDGE,{"derivedFrom":makeQuery(id+"F9.opExtrude","SWEPT_EDGE",EDGE,{"disambiguationData":[OSD([sQuery(id+"F8.wireOp",EDGE,"E19.12.3"),sQuery(id+"F8.wireOp",EDGE,"E21.13.0")])]})});
            var Q78;
            Q78=makeQuery(id+"F9.boolean.opBoolean","COPY",EDGE,{"derivedFrom":makeQuery(id+"F9.opExtrude","SWEPT_EDGE",EDGE,{"disambiguationData":[OSD([sQuery(id+"F8.wireOp",EDGE,"E19.11.0"),sQuery(id+"F8.wireOp",EDGE,"E21.13.0")])]})});
            var Q79;
            Q79=makeQuery(id+"F9.boolean.opBoolean","COPY",EDGE,{"derivedFrom":makeQuery(id+"F9.opExtrude","SWEPT_EDGE",EDGE,{"disambiguationData":[OSD([sQuery(id+"F8.wireOp",EDGE,"E13.0.0"),sQuery(id+"F8.wireOp",EDGE,"E19.11.0"),sQuery(id+"F8.wireOp",EDGE,"E19.11.1")])]})});
            var Q80;
            Q80=makeQuery(id+"F9.boolean.opBoolean","COPY",EDGE,{"derivedFrom":makeQuery(id+"F9.opExtrude","SWEPT_EDGE",EDGE,{"disambiguationData":[OSD([sQuery(id+"F8.wireOp",EDGE,"E13.0.0"),sQuery(id+"F8.wireOp",EDGE,"E19.11.2"),sQuery(id+"F8.wireOp",EDGE,"E19.11.3")])]})});
            var Q81;
            Q81=makeQuery(id+"F9.boolean.opBoolean","COPY",EDGE,{"derivedFrom":makeQuery(id+"F9.opExtrude","SWEPT_EDGE",EDGE,{"disambiguationData":[OSD([sQuery(id+"F8.wireOp",EDGE,"E19.11.3"),sQuery(id+"F8.wireOp",EDGE,"E21.14.0")])]})});
            var Q82;
            Q82=makeQuery(id+"F9.boolean.opBoolean","COPY",EDGE,{"derivedFrom":makeQuery(id+"F9.opExtrude","SWEPT_EDGE",EDGE,{"disambiguationData":[OSD([sQuery(id+"F8.wireOp",EDGE,"E19.10.0"),sQuery(id+"F8.wireOp",EDGE,"E21.14.0")])]})});
            var Q83;
            Q83=makeQuery(id+"F9.boolean.opBoolean","COPY",EDGE,{"derivedFrom":makeQuery(id+"F9.opExtrude","SWEPT_EDGE",EDGE,{"disambiguationData":[OSD([sQuery(id+"F8.wireOp",EDGE,"E13.0.0"),sQuery(id+"F8.wireOp",EDGE,"E19.10.0"),sQuery(id+"F8.wireOp",EDGE,"E19.10.1")])]})});
            var Q84;
            Q84=makeQuery(id+"F9.boolean.opBoolean","COPY",EDGE,{"derivedFrom":makeQuery(id+"F9.opExtrude","SWEPT_EDGE",EDGE,{"disambiguationData":[OSD([sQuery(id+"F8.wireOp",EDGE,"E13.0.0"),sQuery(id+"F8.wireOp",EDGE,"E19.10.2"),sQuery(id+"F8.wireOp",EDGE,"E19.10.3")])]})});
            var Q85;
            Q85=makeQuery(id+"F9.boolean.opBoolean","COPY",EDGE,{"derivedFrom":makeQuery(id+"F9.opExtrude","SWEPT_EDGE",EDGE,{"disambiguationData":[OSD([sQuery(id+"F8.wireOp",EDGE,"E19.10.3"),sQuery(id+"F8.wireOp",EDGE,"E21.15.0")])]})});
            var Q86;
            Q86=makeQuery(id+"F9.boolean.opBoolean","COPY",EDGE,{"derivedFrom":makeQuery(id+"F9.opExtrude","SWEPT_EDGE",EDGE,{"disambiguationData":[OSD([sQuery(id+"F8.wireOp",EDGE,"E19.9.0"),sQuery(id+"F8.wireOp",EDGE,"E21.15.0")])]})});
            var Q87;
            Q87=makeQuery(id+"F9.boolean.opBoolean","COPY",EDGE,{"derivedFrom":makeQuery(id+"F9.opExtrude","SWEPT_EDGE",EDGE,{"disambiguationData":[OSD([sQuery(id+"F8.wireOp",EDGE,"E13.0.0"),sQuery(id+"F8.wireOp",EDGE,"E19.9.0"),sQuery(id+"F8.wireOp",EDGE,"E19.9.1")])]})});
            var Q88;
            Q88=makeQuery(id+"F9.boolean.opBoolean","COPY",EDGE,{"derivedFrom":makeQuery(id+"F9.opExtrude","SWEPT_EDGE",EDGE,{"disambiguationData":[OSD([sQuery(id+"F8.wireOp",EDGE,"E13.0.0"),sQuery(id+"F8.wireOp",EDGE,"E19.9.2"),sQuery(id+"F8.wireOp",EDGE,"E19.9.3")])]})});
            var Q89;
            Q89=makeQuery(id+"F9.boolean.opBoolean","COPY",EDGE,{"derivedFrom":makeQuery(id+"F9.opExtrude","SWEPT_EDGE",EDGE,{"disambiguationData":[OSD([sQuery(id+"F8.wireOp",EDGE,"E19.9.3"),sQuery(id+"F8.wireOp",EDGE,"E21.16.0")])]})});
            var Q90;
            Q90=makeQuery(id+"F9.boolean.opBoolean","COPY",EDGE,{"derivedFrom":makeQuery(id+"F9.opExtrude","SWEPT_EDGE",EDGE,{"disambiguationData":[OSD([sQuery(id+"F8.wireOp",EDGE,"E19.8.0"),sQuery(id+"F8.wireOp",EDGE,"E21.16.0")])]})});
            var Q91;
            Q91=makeQuery(id+"F9.boolean.opBoolean","COPY",EDGE,{"derivedFrom":makeQuery(id+"F9.opExtrude","SWEPT_EDGE",EDGE,{"disambiguationData":[OSD([sQuery(id+"F8.wireOp",EDGE,"E13.0.0"),sQuery(id+"F8.wireOp",EDGE,"E19.8.0"),sQuery(id+"F8.wireOp",EDGE,"E19.8.1")])]})});
            var Q92;
            Q92=makeQuery(id+"F9.boolean.opBoolean","COPY",EDGE,{"derivedFrom":makeQuery(id+"F9.opExtrude","SWEPT_EDGE",EDGE,{"disambiguationData":[OSD([sQuery(id+"F8.wireOp",EDGE,"E13.0.0"),sQuery(id+"F8.wireOp",EDGE,"E19.8.2"),sQuery(id+"F8.wireOp",EDGE,"E19.8.3")])]})});
            var Q93;
            Q93=makeQuery(id+"F9.boolean.opBoolean","COPY",EDGE,{"derivedFrom":makeQuery(id+"F9.opExtrude","SWEPT_EDGE",EDGE,{"disambiguationData":[OSD([sQuery(id+"F8.wireOp",EDGE,"E19.8.3"),sQuery(id+"F8.wireOp",EDGE,"E21.17.0")])]})});
            var Q94;
            Q94=makeQuery(id+"F9.boolean.opBoolean","COPY",EDGE,{"derivedFrom":makeQuery(id+"F9.opExtrude","SWEPT_EDGE",EDGE,{"disambiguationData":[OSD([sQuery(id+"F8.wireOp",EDGE,"E13.0.0"),sQuery(id+"F8.wireOp",EDGE,"E19.7.0"),sQuery(id+"F8.wireOp",EDGE,"E19.7.1")])]})});
            fillet(context, id + "F10", {"entities" : qUnion([Q0, Q1, Q2, Q3, Q4, Q5, Q6, Q7, Q8, Q9, Q10, Q11, Q12, Q13, Q14, Q15, Q16, Q17, Q18, Q19, Q20, Q21, Q22, Q23, Q24, Q25, Q26, Q27, Q28, Q29, Q30, Q31, Q32, Q33, Q34, Q35, Q36, Q37, Q38, Q39, Q40, Q41, Q42, Q43, Q44, Q45, Q46, Q47, Q48, Q49, Q50, Q51, Q52, Q53, Q54, Q55, Q56, Q57, Q58, Q59, Q60, Q61, Q62, Q63, Q64, Q65, Q66, Q67, Q68, Q69, Q70, Q71, Q72, Q73, Q74, Q75, Q76, Q77, Q78, Q79, Q80, Q81, Q82, Q83, Q84, Q85, Q86, Q87, Q88, Q89, Q90, Q91, Q92, Q93, Q94]), "radius" : .75 * mm, "tangentPropagation" : true, "allowEdgeOverflow" : false});
        }
    });
